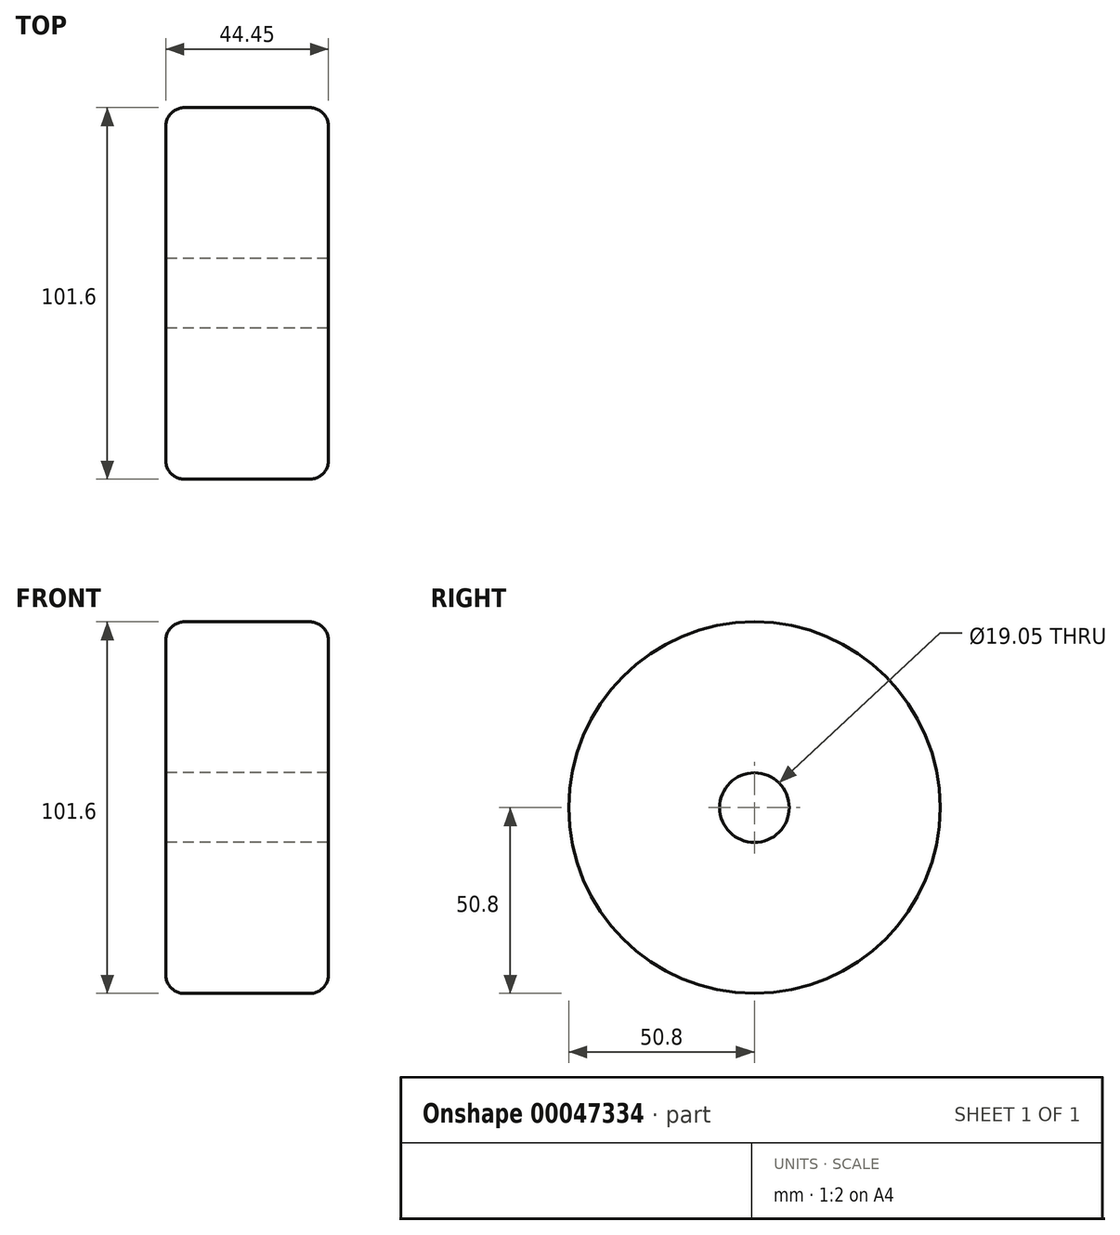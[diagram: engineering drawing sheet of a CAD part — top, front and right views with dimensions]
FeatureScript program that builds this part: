
annotation { "Feature Type Name" : "Feature", "Feature Type Description" : "" }
export const myFeature = defineFeature(function(context is Context, id is Id, definition is map)
    precondition{}
    {
        {
            var Q0;
            Q0=qCreatedBy(makeId("Right.planeOp"),FACE);
            var sketch = newSketch(context, id + "F0", { "sketchPlane" : qUnion([Q0])});
            skCircle(sketch, "E0", {"center": v(0, 0) * mm, "radius": 50.8 * mm});
            skCircle(sketch, "E1", {"center": v(0, 0) * mm, "radius": 9.53 * mm});
            skSolve(sketch);
        }
        {
            var Q0;
            Q0=makeQuery(id+"F0.imprint","IMPRINT",FACE,{"disambiguationData":[TD([[makeQuery(id+"F0.imprint","IMPRINT",EDGE,{"derivedFrom":sQuery(id+"F0.wireOp",EDGE,"E0")}),1.0]])]});
            extrude(context, id + "F1", {"entities" : qUnion([Q0]), "depth" : 44.45 * mm});
        }
        {
            var Q0;
            Q0=makeQuery(id+"F1.opExtrude","CAP_EDGE",EDGE,{"disambiguationData":[OSD([sQuery(id+"F0.wireOp",EDGE,"E0")])],"isStart":false});
            fillet(context, id + "F2", {"entities" : qUnion([Q0]), "radius" : 5.08 * mm, "tangentPropagation" : true, "allowEdgeOverflow" : false});
        }
        {
            var Q0;
            Q0=makeQuery(id+"F1.opExtrude","CAP_EDGE",EDGE,{"disambiguationData":[OSD([sQuery(id+"F0.wireOp",EDGE,"E0")])],"isStart":true});
            fillet(context, id + "F3", {"entities" : qUnion([Q0]), "radius" : 5.08 * mm, "tangentPropagation" : true, "allowEdgeOverflow" : false});
        }
    });
